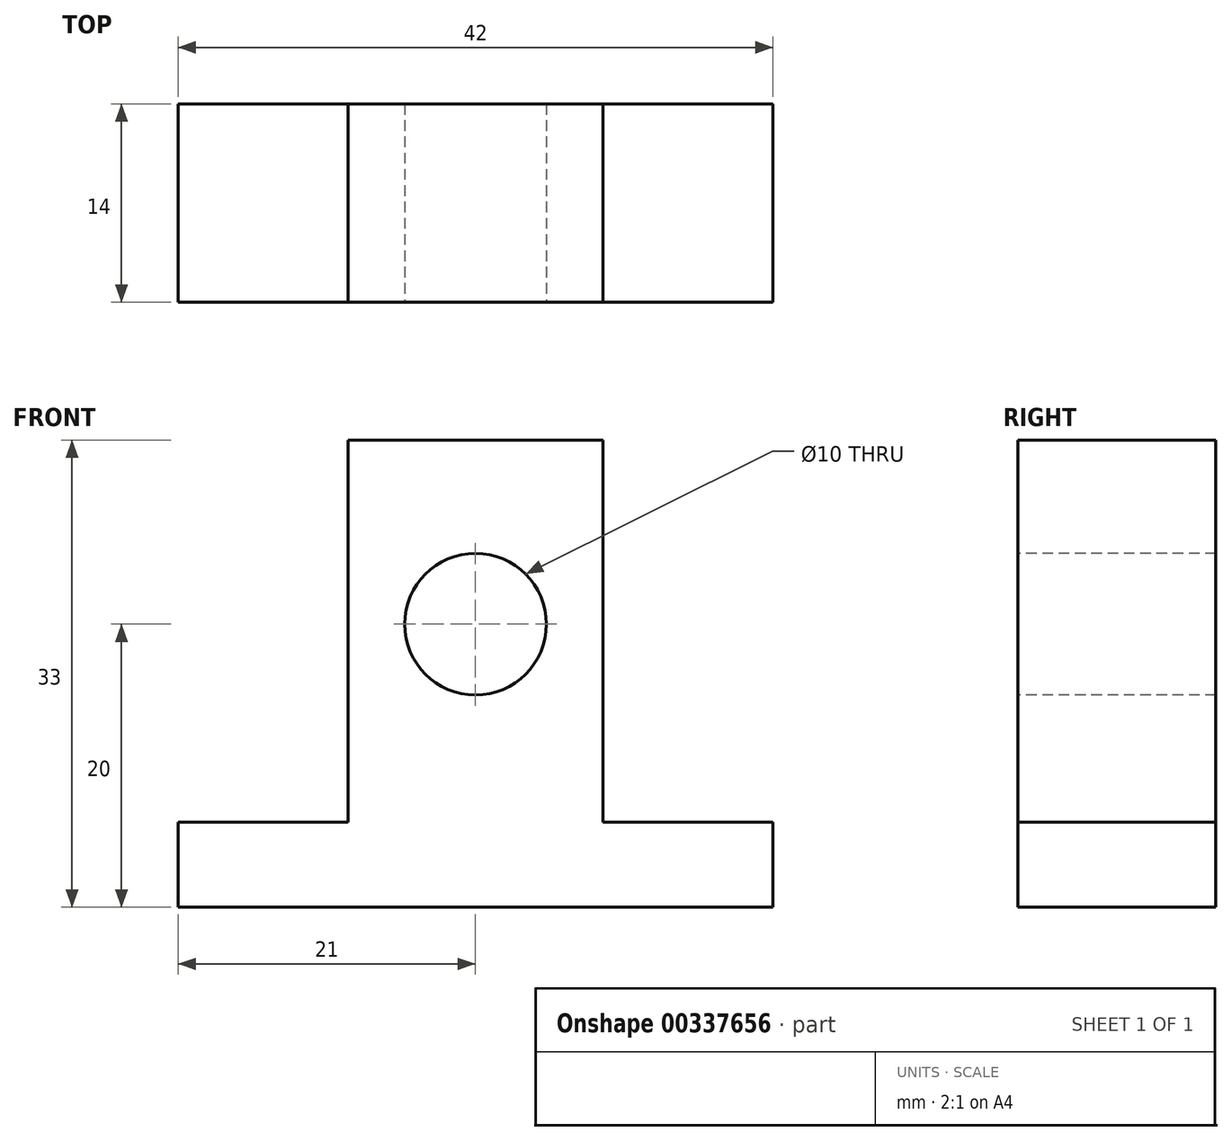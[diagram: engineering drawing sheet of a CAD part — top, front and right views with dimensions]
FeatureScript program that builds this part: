
annotation { "Feature Type Name" : "Feature", "Feature Type Description" : "" }
export const myFeature = defineFeature(function(context is Context, id is Id, definition is map)
    precondition{}
    {
        {
            var Q0;
            Q0=qCreatedBy(makeId("Top.planeOp"),FACE);
            var sketch = newSketch(context, id + "F0", { "sketchPlane" : qUnion([Q0])});
            skLineSegment(sketch, "E0.bottom", {"start": v(21, -7) * mm, "end": v(-21, -7) * mm});
            skLineSegment(sketch, "E0.top", {"start": v(21, 7) * mm, "end": v(-21, 7) * mm});
            skLineSegment(sketch, "E0.left", {"start": v(21, -7) * mm, "end": v(21, 7) * mm});
            skLineSegment(sketch, "E0.right", {"start": v(-21, -7) * mm, "end": v(-21, 7) * mm});
            skPoint(sketch, "E0.middle", {"position": v(0, 0) * mm});
            skSolve(sketch);
        }
        {
            var Q0;
            Q0=makeQuery(id+"F0.imprint","IMPRINT",FACE,{"disambiguationData":[TD([[makeQuery(id+"F0.imprint","IMPRINT",EDGE,{"derivedFrom":sQuery(id+"F0.wireOp",EDGE,"E0.bottom")}),-1.0]])]});
            extrude(context, id + "F1", {"entities" : qUnion([Q0]), "depth" : 6 * mm});
        }
        {
            var Q0;
            Q0=makeQuery(id+"F1.opExtrude","CAP_FACE",FACE,{"disambiguationData":[OSD([sQuery(id+"F0.wireOp",EDGE,"E0.bottom"),sQuery(id+"F0.wireOp",EDGE,"E0.top"),sQuery(id+"F0.wireOp",EDGE,"E0.left"),sQuery(id+"F0.wireOp",EDGE,"E0.right")])],"isStart":false});
            var sketch = newSketch(context, id + "F2", { "sketchPlane" : qUnion([Q0])});
            skLineSegment(sketch, "E1.bottom", {"start": v(9, -7) * mm, "end": v(-9, -7) * mm});
            skLineSegment(sketch, "E1.top", {"start": v(9, 7) * mm, "end": v(-9, 7) * mm});
            skLineSegment(sketch, "E1.left", {"start": v(9, -7) * mm, "end": v(9, 7) * mm});
            skLineSegment(sketch, "E1.right", {"start": v(-9, -7) * mm, "end": v(-9, 7) * mm});
            skPoint(sketch, "E1.middle", {"position": v(0, 0) * mm});
            skSolve(sketch);
        }
        {
            var Q0;
            Q0 = qSketchRegion(id + "F2", true);
            extrude(context, id + "F3", {"entities" : qUnion([Q0]), "operationType" : NewBodyOperationType.ADD, "depth" : 27 * mm});
        }
        {
            var Q0;
            Q0=makeQuery(id+"F3.boolean.opBoolean","MERGE",FACE,{"derivedFrom":[makeQuery(id+"F1.opExtrude","SWEPT_FACE",FACE,{"disambiguationData":[OSD([sQuery(id+"F0.wireOp",EDGE,"E0.bottom")])]}),makeQuery(id+"F3.opExtrude","SWEPT_FACE",FACE,{"disambiguationData":[OSD([sQuery(id+"F2.wireOp",EDGE,"E1.bottom")])]})]});
            var sketch = newSketch(context, id + "F4", { "sketchPlane" : qUnion([Q0])});
            skLineSegment(sketch, "E2", {"start": v(0, 0) * mm, "end": v(0, 20) * mm, "construction": true});
            skCircle(sketch, "E3", {"center": v(0, 20) * mm, "radius": 5 * mm});
            skLineSegment(sketch, "E4", {"start": v(0, 0) * mm, "end": v(0, 33) * mm, "construction": true});
            skSolve(sketch);
        }
        {
            var Q0;
            Q0=makeQuery(id+"F4.imprint","IMPRINT",FACE,{"disambiguationData":[TD([[makeQuery(id+"F4.imprint","IMPRINT",EDGE,{"derivedFrom":sQuery(id+"F4.wireOp",EDGE,"E3")}),1.0]])]});
            extrude(context, id + "F5", {"entities" : qUnion([Q0]), "operationType" : NewBodyOperationType.REMOVE, "endBound" : BoundingType.UP_TO_NEXT, "oppositeDirection" : true, "depth" : 25 * mm});
        }
    });
